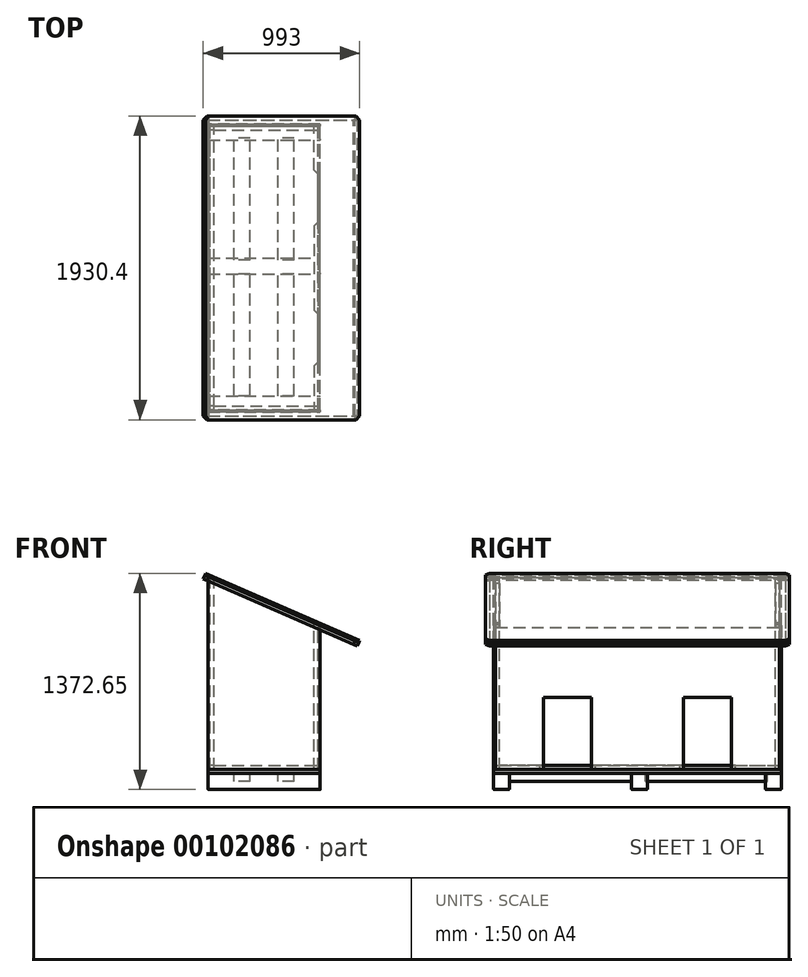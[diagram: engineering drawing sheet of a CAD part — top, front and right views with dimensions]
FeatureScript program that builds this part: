
annotation { "Feature Type Name" : "Feature", "Feature Type Description" : "" }
export const myFeature = defineFeature(function(context is Context, id is Id, definition is map)
    precondition{}
    {
        {
            var Q0;
            Q0=qCreatedBy(makeId("Right.planeOp"),FACE);
            var sketch = newSketch(context, id + "F0", { "sketchPlane" : qUnion([Q0])});
            skLineSegment(sketch, "E0.bottom", {"start": v(0, 0) * mm, "end": v(1803.4, 0) * mm});
            skLineSegment(sketch, "E0.top", {"start": v(0, 1219.2) * mm, "end": v(1803.4, 1219.2) * mm});
            skLineSegment(sketch, "E0.left", {"start": v(0, 0) * mm, "end": v(0, 1219.2) * mm});
            skLineSegment(sketch, "E0.right", {"start": v(1803.4, 0) * mm, "end": v(1803.4, 1219.2) * mm});
            skSolve(sketch);
        }
        {
            var Q0;
            Q0=makeQuery(id+"F0.imprint","IMPRINT",FACE,{"disambiguationData":[TD([[makeQuery(id+"F0.imprint","IMPRINT",EDGE,{"derivedFrom":sQuery(id+"F0.wireOp",EDGE,"E0.bottom")}),1.0]])]});
            extrude(context, id + "F1", {"entities" : qUnion([Q0]), "depth" : 12.7 * mm});
        }
        {
            var Q0;
            Q0=makeQuery(id+"F1.opExtrude","SWEPT_FACE",FACE,{"disambiguationData":[OSD([sQuery(id+"F0.wireOp",EDGE,"E0.right")])]});
            var sketch = newSketch(context, id + "F2", { "sketchPlane" : qUnion([Q0])});
            skLineSegment(sketch, "E1.top", {"start": v(0, 0) * mm, "end": v(-711.2, 0) * mm});
            skLineSegment(sketch, "E1.left", {"start": v(0, 1219.2) * mm, "end": v(0, 0) * mm});
            skLineSegment(sketch, "E1.right", {"start": v(-711.2, 914.4) * mm, "end": v(-711.2, 0) * mm});
            skPoint(sketch, "E2.orphan", {"position": v(-711.2, 1219.2) * mm});
            skLineSegment(sketch, "E3", {"start": v(-711.2, 914.4) * mm, "end": v(-12.7, 1219.2) * mm});
            skLineSegment(sketch, "E4", {"start": v(-12.7, 1219.2) * mm, "end": v(0, 1219.2) * mm});
            skSolve(sketch);
        }
        {
            var Q0;
            Q0 = qSketchRegion(id + "F2", true);
            extrude(context, id + "F3", {"entities" : qUnion([Q0]), "depth" : 12.7 * mm});
        }
        {
            var Q0;
            Q0=makeQuery(id+"F3.opExtrude","SWEPT_BODY",BODY,{"disambiguationData":[OSD([sQuery(id+"F2.wireOp",EDGE,"E1.top"),sQuery(id+"F2.wireOp",EDGE,"E1.left"),sQuery(id+"F2.wireOp",EDGE,"E1.right"),sQuery(id+"F2.wireOp",EDGE,"E3"),sQuery(id+"F2.wireOp",EDGE,"E4")])]});
            transform(context, id + "F4", {"entities" : qUnion([Q0]), "transformType" : TransformType.TRANSLATION_3D, "dx" : 0 * mm, "dy" : -1816.1 * mm, "dz" : 0 * mm, "makeCopy" : true});
        }
        {
            var Q0;
            Q0=qCreatedBy(makeId("Top.planeOp"),FACE);
            var sketch = newSketch(context, id + "F5", { "sketchPlane" : qUnion([Q0])});
            skLineSegment(sketch, "E5.bottom", {"start": v(0, -12.82) * mm, "end": v(711.2, -12.82) * mm});
            skLineSegment(sketch, "E5.top", {"start": v(0, 1815.98) * mm, "end": v(711.2, 1815.98) * mm});
            skLineSegment(sketch, "E5.left", {"start": v(0, -12.82) * mm, "end": v(0, 1815.98) * mm});
            skLineSegment(sketch, "E5.right", {"start": v(711.2, -12.82) * mm, "end": v(711.2, 1815.98) * mm});
            skSolve(sketch);
        }
        {
            var Q0;
            Q0 = qSketchRegion(id + "F5", true);
            extrude(context, id + "F6", {"entities" : qUnion([Q0]), "oppositeDirection" : true, "depth" : 25.4 * mm});
        }
        {
            var Q0;
            Q0=makeQuery(id+"F3.opExtrude","CAP_FACE",FACE,{"disambiguationData":[OSD([sQuery(id+"F2.wireOp",EDGE,"E1.top"),sQuery(id+"F2.wireOp",EDGE,"E1.left"),sQuery(id+"F2.wireOp",EDGE,"E1.right"),sQuery(id+"F2.wireOp",EDGE,"E3"),sQuery(id+"F2.wireOp",EDGE,"E4")])],"isStart":true});
            var sketch = newSketch(context, id + "F7", { "sketchPlane" : qUnion([Q0])});
            skLineSegment(sketch, "E6.bottom", {"start": v(711.2, 0) * mm, "end": v(698.5, 0) * mm});
            skLineSegment(sketch, "E6.top", {"start": v(711.2, 901.7) * mm, "end": v(698.5, 901.7) * mm});
            skLineSegment(sketch, "E6.left", {"start": v(711.2, 0) * mm, "end": v(711.2, 901.7) * mm});
            skLineSegment(sketch, "E6.right", {"start": v(698.5, 0) * mm, "end": v(698.5, 901.7) * mm});
            skSolve(sketch);
        }
        {
            var Q0;
            Q0 = qSketchRegion(id + "F7", true);
            extrude(context, id + "F8", {"entities" : qUnion([Q0]), "depth" : 1803.4 * mm});
        }
        {
            var Q0;
            Q0=makeQuery(id+"F8.opExtrude","SWEPT_FACE",FACE,{"disambiguationData":[OSD([sQuery(id+"F7.wireOp",EDGE,"E6.left")])]});
            var sketch = newSketch(context, id + "F9", { "sketchPlane" : qUnion([Q0])});
            skLineSegment(sketch, "E7.bottom", {"start": v(304.8, 0) * mm, "end": v(609.6, 0) * mm});
            skLineSegment(sketch, "E7.top", {"start": v(304.8, 457.2) * mm, "end": v(609.6, 457.2) * mm});
            skLineSegment(sketch, "E7.left", {"start": v(304.8, 0) * mm, "end": v(304.8, 457.2) * mm});
            skLineSegment(sketch, "E7.right", {"start": v(609.6, 0) * mm, "end": v(609.6, 457.2) * mm});
            skLineSegment(sketch, "E8.bottom", {"start": v(1193.8, 0) * mm, "end": v(1498.6, 0) * mm});
            skLineSegment(sketch, "E8.top", {"start": v(1193.8, 457.2) * mm, "end": v(1498.6, 457.2) * mm});
            skLineSegment(sketch, "E8.left", {"start": v(1193.8, 0) * mm, "end": v(1193.8, 457.2) * mm});
            skLineSegment(sketch, "E8.right", {"start": v(1498.6, 0) * mm, "end": v(1498.6, 457.2) * mm});
            skSolve(sketch);
        }
        {
            var Q0;
            Q0=makeQuery(id+"F9.imprint","IMPRINT",FACE,{"disambiguationData":[TD([[makeQuery(id+"F9.imprint","IMPRINT",EDGE,{"derivedFrom":sQuery(id+"F9.wireOp",EDGE,"E7.bottom")}),1.0]])]});
            var Q1;
            Q1=makeQuery(id+"F9.imprint","IMPRINT",FACE,{"disambiguationData":[TD([[makeQuery(id+"F9.imprint","IMPRINT",EDGE,{"derivedFrom":sQuery(id+"F9.wireOp",EDGE,"E8.bottom")}),1.0]])]});
            extrude(context, id + "F10", {"entities" : qUnion([Q0, Q1]), "operationType" : NewBodyOperationType.REMOVE, "oppositeDirection" : true, "depth" : 12.7 * mm});
        }
        {
            var Q0;
            Q0=makeQuery(id+"F6.opExtrude","CAP_FACE",FACE,{"disambiguationData":[OSD([sQuery(id+"F5.wireOp",EDGE,"E5.bottom"),sQuery(id+"F5.wireOp",EDGE,"E5.top"),sQuery(id+"F5.wireOp",EDGE,"E5.left"),sQuery(id+"F5.wireOp",EDGE,"E5.right")])],"isStart":false});
            var sketch = newSketch(context, id + "F11", { "sketchPlane" : qUnion([Q0])});
            skLineSegment(sketch, "E9.bottom", {"start": v(0, 12.82) * mm, "end": v(711.2, 12.82) * mm});
            skLineSegment(sketch, "E9.top", {"start": v(0, -88.78) * mm, "end": v(711.2, -88.78) * mm});
            skLineSegment(sketch, "E9.left", {"start": v(0, 12.82) * mm, "end": v(0, -88.78) * mm});
            skLineSegment(sketch, "E9.right", {"start": v(711.2, 12.82) * mm, "end": v(711.2, -88.78) * mm});
            skSolve(sketch);
        }
        {
            var Q0;
            Q0 = qSketchRegion(id + "F11", true);
            extrude(context, id + "F12", {"entities" : qUnion([Q0]), "depth" : 101.6 * mm});
        }
        {
            var Q0;
            Q0=makeQuery(id+"F12.opExtrude","CAP_EDGE",EDGE,{"disambiguationData":[OSD([sQuery(id+"F11.wireOp",EDGE,"E9.bottom")])],"isStart":false});
            var Q1;
            Q1=makeQuery(id+"F12.opExtrude","CAP_EDGE",EDGE,{"disambiguationData":[OSD([sQuery(id+"F11.wireOp",EDGE,"E9.top")])],"isStart":false});
            var Q2;
            Q2=makeQuery(id+"F12.opExtrude","CAP_EDGE",EDGE,{"disambiguationData":[OSD([sQuery(id+"F11.wireOp",EDGE,"E9.top")])],"isStart":true});
            var Q3;
            Q3=makeQuery(id+"F12.opExtrude","CAP_EDGE",EDGE,{"disambiguationData":[OSD([sQuery(id+"F11.wireOp",EDGE,"E9.bottom")])],"isStart":true});
            fillet(context, id + "F13", {"entities" : qUnion([Q0, Q1, Q2, Q3]), "radius" : 5.08 * mm, "tangentPropagation" : true, "allowEdgeOverflow" : false});
        }
        {
            var Q0;
            Q0=makeQuery(id+"F12.opExtrude","SWEPT_BODY",BODY,{"disambiguationData":[OSD([sQuery(id+"F11.wireOp",EDGE,"E9.bottom"),sQuery(id+"F11.wireOp",EDGE,"E9.top"),sQuery(id+"F11.wireOp",EDGE,"E9.left"),sQuery(id+"F11.wireOp",EDGE,"E9.right")])]});
            transform(context, id + "F14", {"entities" : qUnion([Q0]), "transformType" : TransformType.TRANSLATION_3D, "dx" : 0 * mm, "dy" : 876.3 * mm, "dz" : 0 * mm, "makeCopy" : true});
        }
        {
            var Q0;
            Q0=makeQuery(id+"F12.opExtrude","SWEPT_BODY",BODY,{"disambiguationData":[OSD([sQuery(id+"F11.wireOp",EDGE,"E9.bottom"),sQuery(id+"F11.wireOp",EDGE,"E9.top"),sQuery(id+"F11.wireOp",EDGE,"E9.left"),sQuery(id+"F11.wireOp",EDGE,"E9.right")])]});
            transform(context, id + "F15", {"entities" : qUnion([Q0]), "transformType" : TransformType.TRANSLATION_3D, "dx" : 0 * mm, "dy" : 1727.2 * mm, "dz" : 0 * mm, "makeCopy" : true});
        }
        {
            var Q0;
            Q0=makeQuery(id+"F1.opExtrude","CAP_FACE",FACE,{"disambiguationData":[OSD([sQuery(id+"F0.wireOp",EDGE,"E0.bottom"),sQuery(id+"F0.wireOp",EDGE,"E0.top"),sQuery(id+"F0.wireOp",EDGE,"E0.left"),sQuery(id+"F0.wireOp",EDGE,"E0.right")])],"isStart":false});
            var sketch = newSketch(context, id + "F16", { "sketchPlane" : qUnion([Q0])});
            skLineSegment(sketch, "E10.bottom", {"start": v(0, 0) * mm, "end": v(25.4, 0) * mm});
            skLineSegment(sketch, "E10.top", {"start": v(0, 1219.2) * mm, "end": v(25.4, 1219.2) * mm});
            skLineSegment(sketch, "E10.left", {"start": v(0, 0) * mm, "end": v(0, 1219.2) * mm});
            skLineSegment(sketch, "E10.right", {"start": v(25.4, 0) * mm, "end": v(25.4, 1219.2) * mm});
            skSolve(sketch);
        }
        {
            var Q0;
            Q0=makeQuery(id+"F16.imprint","IMPRINT",FACE,{"disambiguationData":[TD([[makeQuery(id+"F16.imprint","IMPRINT",EDGE,{"derivedFrom":sQuery(id+"F16.wireOp",EDGE,"E10.bottom")}),1.0]])]});
            extrude(context, id + "F17", {"entities" : qUnion([Q0]), "depth" : 25.4 * mm});
        }
        {
            var Q0;
            Q0=makeQuery(id+"F17.opExtrude","CAP_EDGE",EDGE,{"disambiguationData":[OSD([sQuery(id+"F16.wireOp",EDGE,"E10.top")])],"isStart":false});
            chamfer(context, id + "F18", {"entities" : qUnion([Q0]), "chamferType" : ChamferType.TWO_OFFSETS, "width1" : 25.4 * mm, "oppositeDirection" : false, "width2" : 8.64 * mm, "tangentPropagation" : true});
        }
        {
            var Q0;
            Q0=makeQuery(id+"F17.opExtrude","SWEPT_BODY",BODY,{"disambiguationData":[OSD([sQuery(id+"F16.wireOp",EDGE,"E10.bottom"),sQuery(id+"F16.wireOp",EDGE,"E10.top"),sQuery(id+"F16.wireOp",EDGE,"E10.left"),sQuery(id+"F16.wireOp",EDGE,"E10.right")])]});
            transform(context, id + "F19", {"entities" : qUnion([Q0]), "transformType" : TransformType.TRANSLATION_3D, "dx" : 0 * mm, "dy" : 1778 * mm, "dz" : 0 * mm, "makeCopy" : true});
        }
        {
            var Q0;
            Q0=makeQuery(id+"F1.opExtrude","CAP_FACE",FACE,{"disambiguationData":[OSD([sQuery(id+"F0.wireOp",EDGE,"E0.bottom"),sQuery(id+"F0.wireOp",EDGE,"E0.top"),sQuery(id+"F0.wireOp",EDGE,"E0.left"),sQuery(id+"F0.wireOp",EDGE,"E0.right")])],"isStart":false});
            var sketch = newSketch(context, id + "F20", { "sketchPlane" : qUnion([Q0])});
            skLineSegment(sketch, "E11.bottom", {"start": v(25.4, 0) * mm, "end": v(1778, 0) * mm});
            skLineSegment(sketch, "E11.top", {"start": v(25.4, 25.4) * mm, "end": v(1778, 25.4) * mm});
            skLineSegment(sketch, "E11.left", {"start": v(25.4, 0) * mm, "end": v(25.4, 25.4) * mm});
            skLineSegment(sketch, "E11.right", {"start": v(1778, 0) * mm, "end": v(1778, 25.4) * mm});
            skSolve(sketch);
        }
        {
            var Q0;
            Q0 = qSketchRegion(id + "F20", true);
            extrude(context, id + "F21", {"entities" : qUnion([Q0]), "depth" : 25.4 * mm});
        }
        {
            var Q0;
            Q0=makeQuery(id+"F8.opExtrude","SWEPT_FACE",FACE,{"disambiguationData":[OSD([sQuery(id+"F7.wireOp",EDGE,"E6.right")])]});
            var sketch = newSketch(context, id + "F22", { "sketchPlane" : qUnion([Q0])});
            skLineSegment(sketch, "E12.bottom", {"start": v(-1803.4, 0) * mm, "end": v(-1778, 0) * mm});
            skLineSegment(sketch, "E12.top", {"start": v(-1803.4, 927.1) * mm, "end": v(-1778, 927.1) * mm});
            skLineSegment(sketch, "E12.left", {"start": v(-1803.4, 0) * mm, "end": v(-1803.4, 927.1) * mm});
            skLineSegment(sketch, "E12.right", {"start": v(-1778, 0) * mm, "end": v(-1778, 927.1) * mm});
            skSolve(sketch);
        }
        {
            var Q0;
            Q0 = qSketchRegion(id + "F22", true);
            extrude(context, id + "F23", {"entities" : qUnion([Q0]), "depth" : 25.4 * mm});
        }
        {
            var Q0;
            Q0=makeQuery(id+"F23.opExtrude","CAP_EDGE",EDGE,{"disambiguationData":[OSD([sQuery(id+"F22.wireOp",EDGE,"E12.top")])],"isStart":true});
            chamfer(context, id + "F24", {"entities" : qUnion([Q0]), "chamferType" : ChamferType.TWO_OFFSETS, "width1" : 8.64 * mm, "oppositeDirection" : false, "width2" : 25.4 * mm, "tangentPropagation" : true});
        }
        {
            var Q0;
            Q0=makeQuery(id+"F23.opExtrude","SWEPT_BODY",BODY,{"disambiguationData":[OSD([sQuery(id+"F22.wireOp",EDGE,"E12.bottom"),sQuery(id+"F22.wireOp",EDGE,"E12.top"),sQuery(id+"F22.wireOp",EDGE,"E12.left"),sQuery(id+"F22.wireOp",EDGE,"E12.right")])]});
            transform(context, id + "F25", {"entities" : qUnion([Q0]), "transformType" : TransformType.TRANSLATION_3D, "dx" : 0 * mm, "dy" : -1778 * mm, "dz" : 0 * mm, "makeCopy" : true});
        }
        {
            var Q0;
            Q0=makeQuery(id+"F8.opExtrude","SWEPT_FACE",FACE,{"disambiguationData":[OSD([sQuery(id+"F7.wireOp",EDGE,"E6.right")])]});
            var sketch = newSketch(context, id + "F26", { "sketchPlane" : qUnion([Q0])});
            skLineSegment(sketch, "E13.bottom", {"start": v(-1498.6, 0) * mm, "end": v(-1778, 0) * mm});
            skLineSegment(sketch, "E13.top", {"start": v(-1498.6, 25.4) * mm, "end": v(-1778, 25.4) * mm});
            skLineSegment(sketch, "E13.left", {"start": v(-1498.6, 0) * mm, "end": v(-1498.6, 25.4) * mm});
            skLineSegment(sketch, "E13.right", {"start": v(-1778, 0) * mm, "end": v(-1778, 25.4) * mm});
            skSolve(sketch);
        }
        {
            var Q0;
            Q0 = qSketchRegion(id + "F26", true);
            extrude(context, id + "F27", {"entities" : qUnion([Q0]), "depth" : 25.4 * mm});
        }
        {
            var Q0;
            Q0=makeQuery(id+"F27.opExtrude","CAP_EDGE",EDGE,{"disambiguationData":[OSD([sQuery(id+"F26.wireOp",EDGE,"E13.left")])],"isStart":false});
            chamfer(context, id + "F28", {"entities" : qUnion([Q0]), "width" : 25.4 * mm, "tangentPropagation" : true});
        }
        {
            var Q0;
            Q0=makeQuery(id+"F8.opExtrude","SWEPT_FACE",FACE,{"disambiguationData":[OSD([sQuery(id+"F7.wireOp",EDGE,"E6.right")])]});
            var sketch = newSketch(context, id + "F29", { "sketchPlane" : qUnion([Q0])});
            skLineSegment(sketch, "E14.bottom", {"start": v(-1193.8, 0) * mm, "end": v(-609.6, 0) * mm});
            skLineSegment(sketch, "E14.top", {"start": v(-1193.8, 25.4) * mm, "end": v(-609.6, 25.4) * mm});
            skLineSegment(sketch, "E14.left", {"start": v(-1193.8, 0) * mm, "end": v(-1193.8, 25.4) * mm});
            skLineSegment(sketch, "E14.right", {"start": v(-609.6, 0) * mm, "end": v(-609.6, 25.4) * mm});
            skSolve(sketch);
        }
        {
            var Q0;
            Q0 = qSketchRegion(id + "F29", true);
            extrude(context, id + "F30", {"entities" : qUnion([Q0]), "depth" : 25.4 * mm});
        }
        {
            var Q0;
            Q0=makeQuery(id+"F30.opExtrude","CAP_EDGE",EDGE,{"disambiguationData":[OSD([sQuery(id+"F29.wireOp",EDGE,"E14.left")])],"isStart":false});
            var Q1;
            Q1=makeQuery(id+"F30.opExtrude","CAP_EDGE",EDGE,{"disambiguationData":[OSD([sQuery(id+"F29.wireOp",EDGE,"E14.right")])],"isStart":false});
            chamfer(context, id + "F31", {"entities" : qUnion([Q0, Q1]), "width" : 25.4 * mm, "tangentPropagation" : true});
        }
        {
            var Q0;
            Q0=makeQuery(id+"F8.opExtrude","SWEPT_FACE",FACE,{"disambiguationData":[OSD([sQuery(id+"F7.wireOp",EDGE,"E6.right")])]});
            var sketch = newSketch(context, id + "F32", { "sketchPlane" : qUnion([Q0])});
            skLineSegment(sketch, "E15.bottom", {"start": v(-304.8, 0) * mm, "end": v(-25.4, 0) * mm});
            skLineSegment(sketch, "E15.top", {"start": v(-304.8, 25.4) * mm, "end": v(-25.4, 25.4) * mm});
            skLineSegment(sketch, "E15.left", {"start": v(-304.8, 0) * mm, "end": v(-304.8, 25.4) * mm});
            skLineSegment(sketch, "E15.right", {"start": v(-25.4, 0) * mm, "end": v(-25.4, 25.4) * mm});
            skSolve(sketch);
        }
        {
            var Q0;
            Q0 = qSketchRegion(id + "F32", true);
            extrude(context, id + "F33", {"entities" : qUnion([Q0]), "depth" : 25.4 * mm});
        }
        {
            var Q0;
            Q0=makeQuery(id+"F33.opExtrude","CAP_EDGE",EDGE,{"disambiguationData":[OSD([sQuery(id+"F32.wireOp",EDGE,"E15.left")])],"isStart":false});
            chamfer(context, id + "F34", {"entities" : qUnion([Q0]), "width" : 25.4 * mm, "tangentPropagation" : true});
        }
        {
            var Q0;
            Q0=makeQuery(id+"F3.opExtrude","CAP_FACE",FACE,{"disambiguationData":[OSD([sQuery(id+"F2.wireOp",EDGE,"E1.top"),sQuery(id+"F2.wireOp",EDGE,"E1.left"),sQuery(id+"F2.wireOp",EDGE,"E1.right"),sQuery(id+"F2.wireOp",EDGE,"E3"),sQuery(id+"F2.wireOp",EDGE,"E4")])],"isStart":true});
            var sketch = newSketch(context, id + "F35", { "sketchPlane" : qUnion([Q0])});
            skLineSegment(sketch, "E16.bottom", {"start": v(38.1, 0) * mm, "end": v(673.1, 0) * mm});
            skLineSegment(sketch, "E16.top", {"start": v(38.1, 25.4) * mm, "end": v(673.1, 25.4) * mm});
            skLineSegment(sketch, "E16.left", {"start": v(38.1, 0) * mm, "end": v(38.1, 25.4) * mm});
            skLineSegment(sketch, "E16.right", {"start": v(673.1, 0) * mm, "end": v(673.1, 25.4) * mm});
            skSolve(sketch);
        }
        {
            var Q0;
            Q0 = qSketchRegion(id + "F35", true);
            extrude(context, id + "F36", {"entities" : qUnion([Q0]), "depth" : 25.4 * mm});
        }
        {
            var Q0;
            Q0=makeQuery(id+"F36.opExtrude","SWEPT_BODY",BODY,{"disambiguationData":[OSD([sQuery(id+"F35.wireOp",EDGE,"E16.bottom"),sQuery(id+"F35.wireOp",EDGE,"E16.top"),sQuery(id+"F35.wireOp",EDGE,"E16.left"),sQuery(id+"F35.wireOp",EDGE,"E16.right")])]});
            transform(context, id + "F37", {"entities" : qUnion([Q0]), "transformType" : TransformType.TRANSLATION_3D, "dx" : 0 * mm, "dy" : -1778 * mm, "dz" : 0 * mm, "makeCopy" : true});
        }
        {
            var Q0;
            Q0=makeQuery(id+"F4.opPattern","COPY",FACE,{"derivedFrom":makeQuery(id+"F3.opExtrude","SWEPT_FACE",FACE,{"disambiguationData":[OSD([sQuery(id+"F2.wireOp",EDGE,"E3")])]}),"instanceName":"1"});
            var sketch = newSketch(context, id + "F38", { "sketchPlane" : qUnion([Q0])});
            skLineSegment(sketch, "E17.bottom", {"start": v(-513.01, 1866.9) * mm, "end": v(553.79, 1866.9) * mm});
            skLineSegment(sketch, "E17.top", {"start": v(-513.01, -63.5) * mm, "end": v(553.79, -63.5) * mm});
            skLineSegment(sketch, "E17.left", {"start": v(-513.01, 1866.9) * mm, "end": v(-513.01, -63.5) * mm});
            skLineSegment(sketch, "E17.right", {"start": v(553.79, 1866.9) * mm, "end": v(553.79, -63.5) * mm});
            skSolve(sketch);
        }
        {
            var Q0;
            Q0 = qSketchRegion(id + "F38", true);
            extrude(context, id + "F39", {"entities" : qUnion([Q0]), "depth" : 12.7 * mm});
        }
        {
            var Q0;
            Q0=makeQuery(id+"F39.opExtrude","SWEPT_EDGE",EDGE,{"disambiguationData":[OSD([sQuery(id+"F38.wireOp",EDGE,"E17.top"),sQuery(id+"F38.wireOp",EDGE,"E17.right")])]});
            var Q1;
            Q1=makeQuery(id+"F39.opExtrude","SWEPT_EDGE",EDGE,{"disambiguationData":[OSD([sQuery(id+"F38.wireOp",EDGE,"E17.bottom"),sQuery(id+"F38.wireOp",EDGE,"E17.right")])]});
            var Q2;
            Q2=makeQuery(id+"F39.opExtrude","SWEPT_EDGE",EDGE,{"disambiguationData":[OSD([sQuery(id+"F38.wireOp",EDGE,"E17.bottom"),sQuery(id+"F38.wireOp",EDGE,"E17.left")])]});
            var Q3;
            Q3=makeQuery(id+"F39.opExtrude","SWEPT_EDGE",EDGE,{"disambiguationData":[OSD([sQuery(id+"F38.wireOp",EDGE,"E17.top"),sQuery(id+"F38.wireOp",EDGE,"E17.left")])]});
            chamfer(context, id + "F40", {"entities" : qUnion([Q0, Q1, Q2, Q3]), "width" : 25.4 * mm, "tangentPropagation" : true});
        }
        {
            var Q0;
            Q0=makeQuery(id+"F39.opExtrude","CAP_FACE",FACE,{"disambiguationData":[OSD([sQuery(id+"F38.wireOp",EDGE,"E17.bottom"),sQuery(id+"F38.wireOp",EDGE,"E17.top"),sQuery(id+"F38.wireOp",EDGE,"E17.left"),sQuery(id+"F38.wireOp",EDGE,"E17.right")])],"isStart":true});
            var sketch = newSketch(context, id + "F41", { "sketchPlane" : qUnion([Q0])});
            skPoint(sketch, "E18.oppositeSnap0", {"position": v(-513.01, -901.7) * mm});
            skLineSegment(sketch, "E18.bottom", {"start": v(-487.61, -1866.9) * mm, "end": v(-513.01, -1866.9) * mm});
            skLineSegment(sketch, "E18.top", {"start": v(-487.61, 63.5) * mm, "end": v(-513.01, 63.5) * mm});
            skLineSegment(sketch, "E18.left", {"start": v(-487.61, -1866.9) * mm, "end": v(-487.61, 63.5) * mm});
            skLineSegment(sketch, "E18.right", {"start": v(-513.01, -1866.9) * mm, "end": v(-513.01, 63.5) * mm});
            skSolve(sketch);
        }
        {
            var Q0;
            Q0 = qSketchRegion(id + "F41", true);
            extrude(context, id + "F42", {"entities" : qUnion([Q0]), "depth" : 25.4 * mm});
        }
        {
            var Q0;
            Q0=makeQuery(id+"F42.opExtrude","SWEPT_EDGE",EDGE,{"disambiguationData":[OSD([sQuery(id+"F41.wireOp",EDGE,"E18.bottom"),sQuery(id+"F41.wireOp",EDGE,"E18.right")])]});
            var Q1;
            Q1=makeQuery(id+"F42.opExtrude","SWEPT_EDGE",EDGE,{"disambiguationData":[OSD([sQuery(id+"F41.wireOp",EDGE,"E18.top"),sQuery(id+"F41.wireOp",EDGE,"E18.right")])]});
            chamfer(context, id + "F43", {"entities" : qUnion([Q0, Q1]), "width" : 25.4 * mm, "tangentPropagation" : true});
        }
        {
            var Q0;
            Q0=makeQuery(id+"F39.opExtrude","CAP_FACE",FACE,{"disambiguationData":[OSD([sQuery(id+"F38.wireOp",EDGE,"E17.bottom"),sQuery(id+"F38.wireOp",EDGE,"E17.top"),sQuery(id+"F38.wireOp",EDGE,"E17.left"),sQuery(id+"F38.wireOp",EDGE,"E17.right")])],"isStart":true});
            var sketch = newSketch(context, id + "F44", { "sketchPlane" : qUnion([Q0])});
            skLineSegment(sketch, "E19.bottom", {"start": v(-487.61, -1866.9) * mm, "end": v(553.79, -1866.9) * mm});
            skLineSegment(sketch, "E19.top", {"start": v(-487.61, -1841.5) * mm, "end": v(553.79, -1841.5) * mm});
            skLineSegment(sketch, "E19.left", {"start": v(-487.61, -1866.9) * mm, "end": v(-487.61, -1841.5) * mm});
            skLineSegment(sketch, "E19.right", {"start": v(553.79, -1866.9) * mm, "end": v(553.79, -1841.5) * mm});
            skSolve(sketch);
        }
        {
            var Q0;
            Q0 = qSketchRegion(id + "F44", true);
            extrude(context, id + "F45", {"entities" : qUnion([Q0]), "depth" : 25.4 * mm});
        }
        {
            var Q0;
            Q0=makeQuery(id+"F45.opExtrude","SWEPT_EDGE",EDGE,{"disambiguationData":[OSD([sQuery(id+"F44.wireOp",EDGE,"E19.bottom"),sQuery(id+"F44.wireOp",EDGE,"E19.right")])]});
            chamfer(context, id + "F46", {"entities" : qUnion([Q0]), "width" : 25.4 * mm, "tangentPropagation" : true});
        }
        {
            var Q0;
            Q0=makeQuery(id+"F39.opExtrude","CAP_FACE",FACE,{"disambiguationData":[OSD([sQuery(id+"F38.wireOp",EDGE,"E17.bottom"),sQuery(id+"F38.wireOp",EDGE,"E17.top"),sQuery(id+"F38.wireOp",EDGE,"E17.left"),sQuery(id+"F38.wireOp",EDGE,"E17.right")])],"isStart":true});
            var sketch = newSketch(context, id + "F47", { "sketchPlane" : qUnion([Q0])});
            skLineSegment(sketch, "E20.bottom", {"start": v(-487.61, 63.5) * mm, "end": v(553.79, 63.5) * mm});
            skLineSegment(sketch, "E20.top", {"start": v(-487.61, 38.1) * mm, "end": v(553.79, 38.1) * mm});
            skLineSegment(sketch, "E20.left", {"start": v(-487.61, 63.5) * mm, "end": v(-487.61, 38.1) * mm});
            skLineSegment(sketch, "E20.right", {"start": v(553.79, 63.5) * mm, "end": v(553.79, 38.1) * mm});
            skSolve(sketch);
        }
        {
            var Q0;
            Q0 = qSketchRegion(id + "F47", true);
            extrude(context, id + "F48", {"entities" : qUnion([Q0]), "depth" : 25.4 * mm});
        }
        {
            var Q0;
            Q0=makeQuery(id+"F48.opExtrude","SWEPT_EDGE",EDGE,{"disambiguationData":[OSD([sQuery(id+"F47.wireOp",EDGE,"E20.bottom"),sQuery(id+"F47.wireOp",EDGE,"E20.right")])]});
            chamfer(context, id + "F49", {"entities" : qUnion([Q0]), "width" : 25.4 * mm, "tangentPropagation" : true});
        }
        {
            var Q0;
            Q0=makeQuery(id+"F39.opExtrude","CAP_FACE",FACE,{"disambiguationData":[OSD([sQuery(id+"F38.wireOp",EDGE,"E17.bottom"),sQuery(id+"F38.wireOp",EDGE,"E17.top"),sQuery(id+"F38.wireOp",EDGE,"E17.left"),sQuery(id+"F38.wireOp",EDGE,"E17.right")])],"isStart":true});
            var sketch = newSketch(context, id + "F50", { "sketchPlane" : qUnion([Q0])});
            skLineSegment(sketch, "E21.bottom", {"start": v(553.79, 38.1) * mm, "end": v(528.39, 38.1) * mm});
            skLineSegment(sketch, "E21.top", {"start": v(553.79, -1841.5) * mm, "end": v(528.39, -1841.5) * mm});
            skLineSegment(sketch, "E21.left", {"start": v(553.79, 38.1) * mm, "end": v(553.79, -1841.5) * mm});
            skLineSegment(sketch, "E21.right", {"start": v(528.39, 38.1) * mm, "end": v(528.39, -1841.5) * mm});
            skSolve(sketch);
        }
        {
            var Q0;
            Q0 = qSketchRegion(id + "F50", true);
            extrude(context, id + "F51", {"entities" : qUnion([Q0]), "depth" : 25.4 * mm});
        }
        {
            var Q0;
            Q0=makeQuery(id+"F4.opPattern","COPY",FACE,{"derivedFrom":makeQuery(id+"F3.opExtrude","CAP_FACE",FACE,{"disambiguationData":[OSD([sQuery(id+"F2.wireOp",EDGE,"E1.top"),sQuery(id+"F2.wireOp",EDGE,"E1.left"),sQuery(id+"F2.wireOp",EDGE,"E1.right"),sQuery(id+"F2.wireOp",EDGE,"E3"),sQuery(id+"F2.wireOp",EDGE,"E4")])],"isStart":false}),"instanceName":"1"});
            var sketch = newSketch(context, id + "F52", { "sketchPlane" : qUnion([Q0])});
            skLineSegment(sketch, "E22", {"start": v(-38.1, 1180.4) * mm, "end": v(-673.1, 903.31) * mm});
            skLineSegment(sketch, "E23", {"start": v(-673.1, 931.03) * mm, "end": v(-38.1, 1208.12) * mm});
            skLineSegment(sketch, "E24", {"start": v(-38.1, 1180.4) * mm, "end": v(-38.1, 1208.12) * mm});
            skLineSegment(sketch, "E25", {"start": v(-673.1, 903.31) * mm, "end": v(-673.1, 931.03) * mm});
            skPoint(sketch, "E26.start.orphan", {"position": v(-868.93, 817.86) * mm});
            skSolve(sketch);
        }
        {
            var Q0;
            Q0 = qSketchRegion(id + "F52", true);
            extrude(context, id + "F53", {"entities" : qUnion([Q0]), "depth" : 25.4 * mm});
        }
        {
            var Q0;
            Q0=makeQuery(id+"F53.opExtrude","SWEPT_BODY",BODY,{"disambiguationData":[OSD([sQuery(id+"F52.wireOp",EDGE,"E22"),sQuery(id+"F52.wireOp",EDGE,"E23"),sQuery(id+"F52.wireOp",EDGE,"E24"),sQuery(id+"F52.wireOp",EDGE,"E25")])]});
            transform(context, id + "F54", {"entities" : qUnion([Q0]), "transformType" : TransformType.TRANSLATION_3D, "dx" : 0 * mm, "dy" : 1778 * mm, "dz" : 0 * mm, "makeCopy" : true});
        }
        {
            var Q0;
            Q0=makeQuery(id+"F6.opExtrude","CAP_FACE",FACE,{"disambiguationData":[OSD([sQuery(id+"F5.wireOp",EDGE,"E5.bottom"),sQuery(id+"F5.wireOp",EDGE,"E5.top"),sQuery(id+"F5.wireOp",EDGE,"E5.left"),sQuery(id+"F5.wireOp",EDGE,"E5.right")])],"isStart":false});
            var sketch = newSketch(context, id + "F55", { "sketchPlane" : qUnion([Q0])});
            skLineSegment(sketch, "E27.bottom", {"start": v(546.1, -88.78) * mm, "end": v(444.5, -88.78) * mm});
            skLineSegment(sketch, "E27.top", {"start": v(546.1, -863.48) * mm, "end": v(444.5, -863.48) * mm});
            skLineSegment(sketch, "E27.left", {"start": v(546.1, -88.78) * mm, "end": v(546.1, -863.48) * mm});
            skLineSegment(sketch, "E27.right", {"start": v(444.5, -88.78) * mm, "end": v(444.5, -863.48) * mm});
            skSolve(sketch);
        }
        {
            var Q0;
            Q0 = qSketchRegion(id + "F55", true);
            extrude(context, id + "F56", {"entities" : qUnion([Q0]), "depth" : 50.8 * mm});
        }
        {
            var Q0;
            Q0=makeQuery(id+"F56.opExtrude","SWEPT_BODY",BODY,{"disambiguationData":[OSD([sQuery(id+"F55.wireOp",EDGE,"E27.bottom"),sQuery(id+"F55.wireOp",EDGE,"E27.top"),sQuery(id+"F55.wireOp",EDGE,"E27.left"),sQuery(id+"F55.wireOp",EDGE,"E27.right")])]});
            transform(context, id + "F57", {"entities" : qUnion([Q0]), "transformType" : TransformType.TRANSLATION_3D, "dx" : -279.4 * mm, "dy" : 0 * mm, "dz" : 0 * mm, "makeCopy" : true});
        }
        {
            var Q0;
            Q0=makeQuery(id+"F56.opExtrude","SWEPT_BODY",BODY,{"disambiguationData":[OSD([sQuery(id+"F55.wireOp",EDGE,"E27.bottom"),sQuery(id+"F55.wireOp",EDGE,"E27.top"),sQuery(id+"F55.wireOp",EDGE,"E27.left"),sQuery(id+"F55.wireOp",EDGE,"E27.right")])]});
            transform(context, id + "F58", {"entities" : qUnion([Q0]), "transformType" : TransformType.TRANSLATION_3D, "dx" : 0 * mm, "dy" : 863.6 * mm, "dz" : 0 * mm, "makeCopy" : true});
        }
        {
            var Q0;
            Q0=makeQuery(id+"F57.opPattern","COPY",BODY,{"derivedFrom":makeQuery(id+"F56.opExtrude","SWEPT_BODY",BODY,{"disambiguationData":[OSD([sQuery(id+"F55.wireOp",EDGE,"E27.bottom"),sQuery(id+"F55.wireOp",EDGE,"E27.top"),sQuery(id+"F55.wireOp",EDGE,"E27.left"),sQuery(id+"F55.wireOp",EDGE,"E27.right")])]}),"instanceName":"1"});
            transform(context, id + "F59", {"entities" : qUnion([Q0]), "transformType" : TransformType.TRANSLATION_3D, "dx" : 0 * mm, "dy" : 863.6 * mm, "dz" : 0 * mm, "makeCopy" : true});
        }
    });
